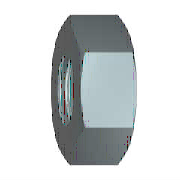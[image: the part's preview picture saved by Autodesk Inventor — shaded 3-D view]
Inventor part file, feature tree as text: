
AUTODESK INVENTOR PART (.ipt)
format: ipt  version: 2015 (Build 190159000, 159)  size: 162,304 bytes
history: native  units: mm (DEFAULTED — no unit token found)
features: sketch x3, chamfer x1, hole x1, other x1, plane x1
ambient origin geometry x7: Origin, YZ Plane, XZ Plane, X Axis, Y Axis, Z Axis, Center Point
bodies: Solid1 (feature_tree), Body (feature_tree)
feature tree (7):
  chamfer  "Chamfer1"  Angle=30.0deg  [1 undecoded]
  hole  "Thread"  [1 undecoded]
  other  "Work Axis1"
  plane  "Work Plane1"
  sketch  "Sketch1"  dims[d0=19.629909mm]
  sketch  "Sketch2"  dims[d1=8.0mm]
  sketch  "Sketch3"  dims[d2=0.0mm d3=30.0deg d4=30.0deg d5=15.3mm d6=15.3mm d7=90.0deg d25=8.376mm d26=6.0mm d27=4.0mm d28=2.0mm d29=14.3117mm d30=8.0mm d31=20.594885mm d8=0.811899mm d9=30.0deg d10=0.811899mm d11=30.0deg d13=0.0mm d14=0.0mm d39=0.0mm d40=0.811899mm d41=0.811899mm d42=0.0mm]
note: 2 required parameter values undecoded (feature->parameter linkage not recoverable at this tier; creation-order binding heuristic only, values carry confidence <= 0.55)
